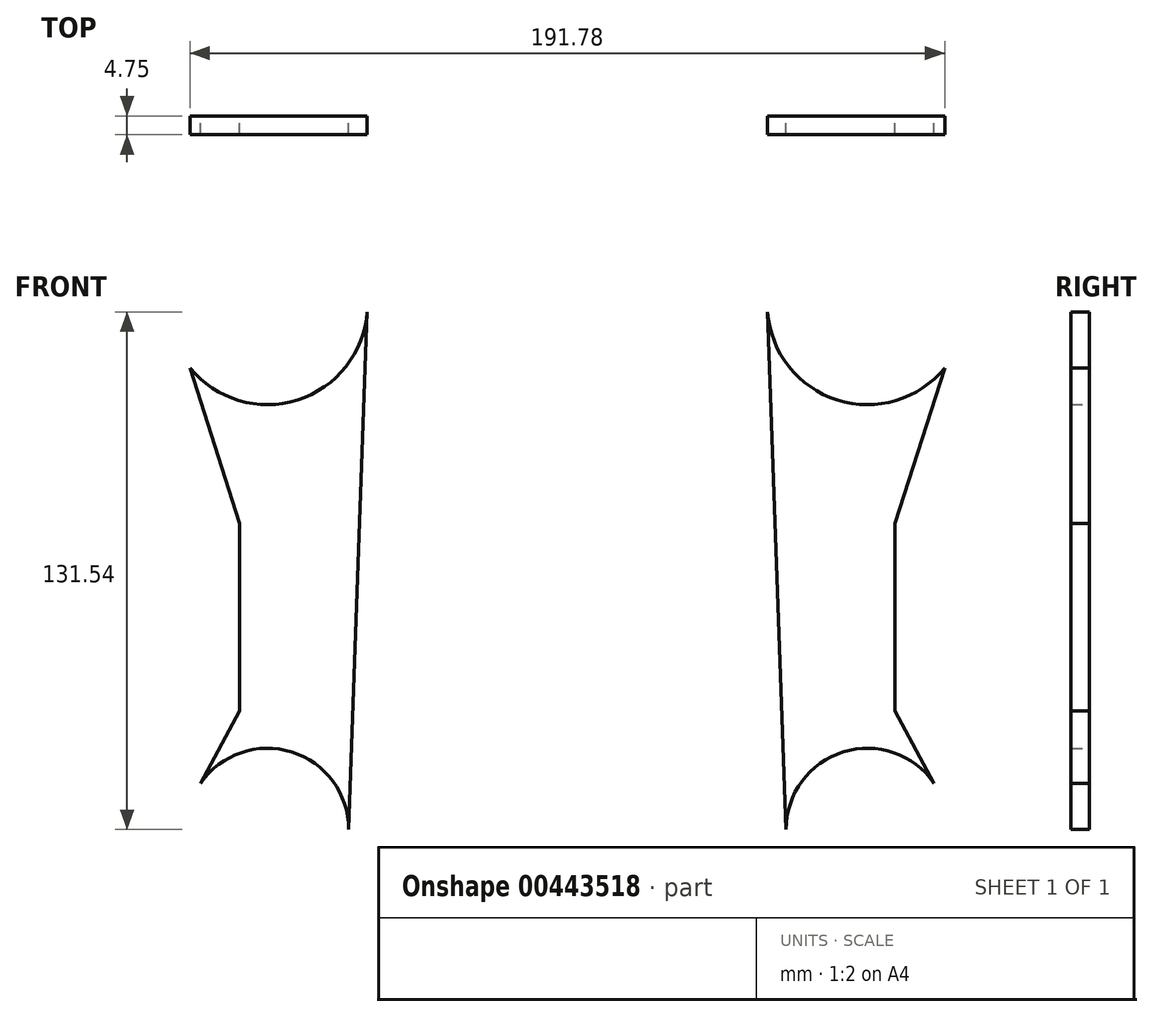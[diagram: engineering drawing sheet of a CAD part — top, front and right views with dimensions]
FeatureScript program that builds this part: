
annotation { "Feature Type Name" : "Feature", "Feature Type Description" : "" }
export const myFeature = defineFeature(function(context is Context, id is Id, definition is map)
    precondition{}
    {
        {
            var Q0;
            Q0=qCreatedBy(makeId("Front.planeOp"),FACE);
            var sketch = newSketch(context, id + "F0", { "sketchPlane" : qUnion([Q0])});
            skCircle(sketch, "E0", {"center": v(-76.2, 82.03) * mm, "radius": 25.4 * mm});
            skCircle(sketch, "E1", {"center": v(-76.2, -51.32) * mm, "radius": 20.64 * mm});
            skCircle(sketch, "E2", {"center": v(-76.2, 82.03) * mm, "radius": 7.15 * mm});
            skCircle(sketch, "E3", {"center": v(-76.2, -51.32) * mm, "radius": 6.29 * mm});
            skCircle(sketch, "E4.MirrorC", {"center": v(76.2, 82.03) * mm, "radius": 25.4 * mm});
            skCircle(sketch, "E5.MirrorC", {"center": v(76.2, -51.32) * mm, "radius": 20.64 * mm});
            skCircle(sketch, "E6.MirrorC", {"center": v(76.2, 82.03) * mm, "radius": 7.15 * mm});
            skCircle(sketch, "E7.MirrorC", {"center": v(76.2, -51.32) * mm, "radius": 6.29 * mm});
            skLineSegment(sketch, "E8", {"start": v(-95.9, 65.99) * mm, "end": v(-83.26, 26.48) * mm});
            skLineSegment(sketch, "E9", {"start": v(-83.26, 26.48) * mm, "end": v(-83.26, -21.2) * mm});
            skLineSegment(sketch, "E10", {"start": v(-83.26, -21.2) * mm, "end": v(-93.17, -39.58) * mm});
            skLineSegment(sketch, "E11.MirrorCS", {"start": v(95.9, 65.99) * mm, "end": v(83.26, 26.48) * mm});
            skLineSegment(sketch, "E12.MirrorCS", {"start": v(83.26, 26.48) * mm, "end": v(83.26, -21.2) * mm});
            skLineSegment(sketch, "E13.MirrorCS", {"start": v(83.26, -21.2) * mm, "end": v(93.17, -39.58) * mm});
            skLineSegment(sketch, "E14", {"start": v(-55.56, -51.32) * mm, "end": v(-50.8, 82.03) * mm});
            skLineSegment(sketch, "E15.MirrorCS", {"start": v(55.56, -51.32) * mm, "end": v(50.8, 82.03) * mm});
            skSolve(sketch);
        }
        {
            var Q0;
            {var subQ0=sQuery(id+"F0.wireOp",EDGE,"E8");Q0=makeQuery(id+"F0.imprint","IMPRINT",FACE,{"disambiguationData":[TD([[makeQuery(id+"F0.imprint","IMPRINT",EDGE,{"derivedFrom":subQ0}),1.0]])]});}
            var Q1;
            {var subQ0=sQuery(id+"F0.wireOp",EDGE,"E11.MirrorCS");Q1=makeQuery(id+"F0.imprint","IMPRINT",FACE,{"disambiguationData":[TD([[makeQuery(id+"F0.imprint","IMPRINT",EDGE,{"derivedFrom":subQ0}),-1.0]])]});}
            extrude(context, id + "F1", {"entities" : qUnion([Q0, Q1]), "depth" : 4.75 * mm});
        }
    });
